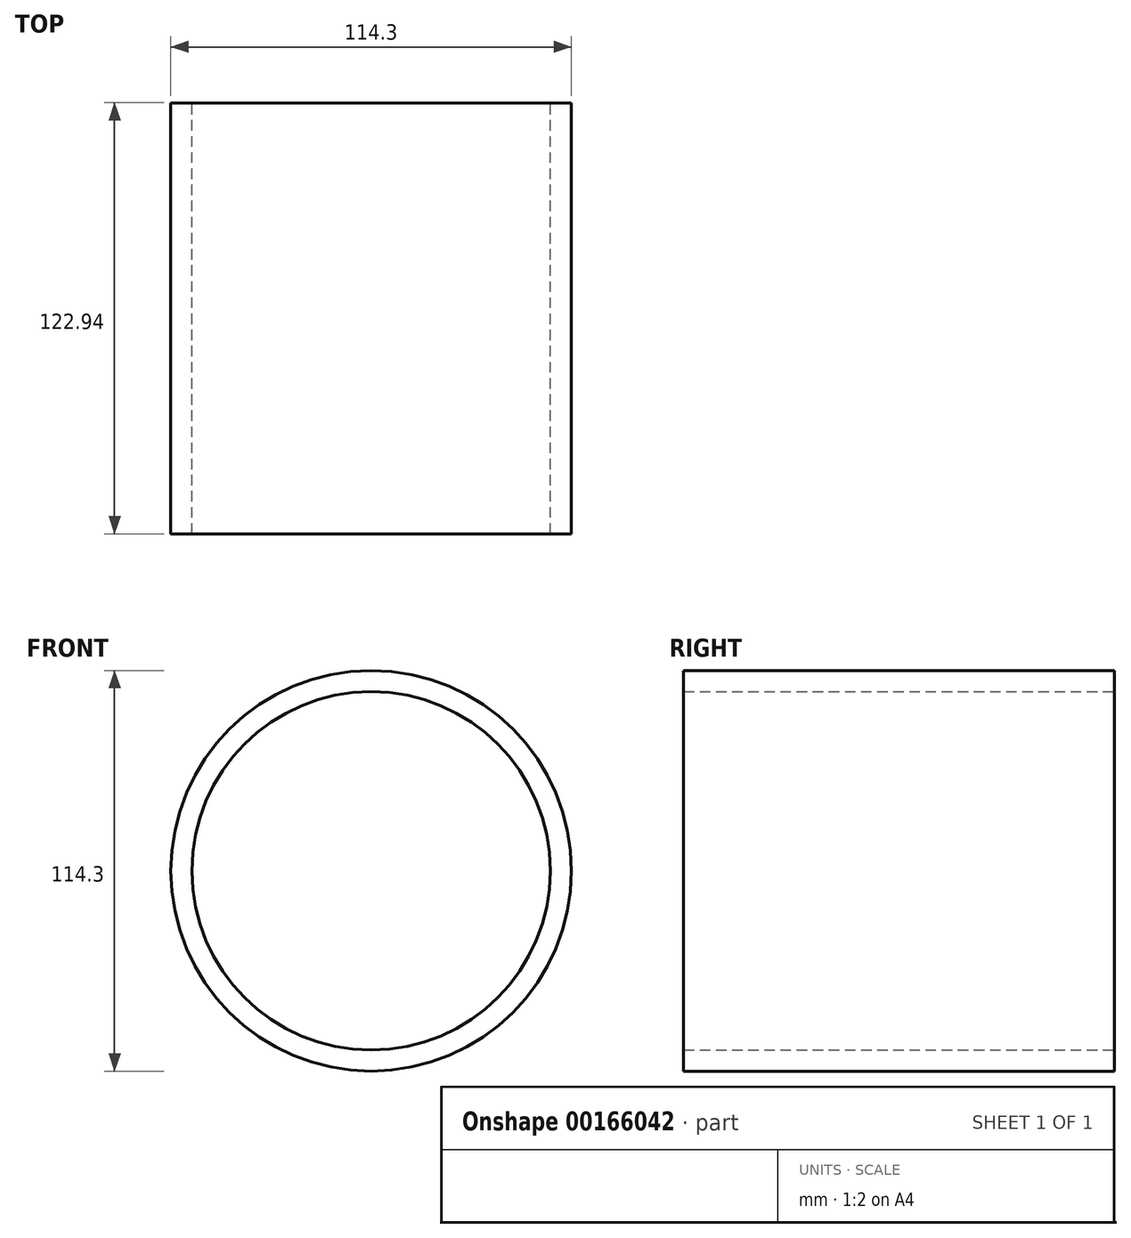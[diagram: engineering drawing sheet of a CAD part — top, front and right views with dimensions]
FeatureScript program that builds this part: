
annotation { "Feature Type Name" : "Feature", "Feature Type Description" : "" }
export const myFeature = defineFeature(function(context is Context, id is Id, definition is map)
    precondition{}
    {
        {
            var Q0;
            Q0=qCreatedBy(makeId("Front.planeOp"),FACE);
            var sketch = newSketch(context, id + "F0", { "sketchPlane" : qUnion([Q0])});
            skCircle(sketch, "E0", {"center": v(0, 0) * mm, "radius": 51.13 * mm});
            skCircle(sketch, "E1", {"center": v(0, 0) * mm, "radius": 57.15 * mm});
            skSolve(sketch);
        }
        {
            var Q0;
            Q0=makeQuery(id+"F0.imprint","IMPRINT",FACE,{"disambiguationData":[TD([[makeQuery(id+"F0.imprint","IMPRINT",EDGE,{"derivedFrom":sQuery(id+"F0.wireOp",EDGE,"E0")}),-1.0]])]});
            extrude(context, id + "F1", {"entities" : qUnion([Q0]), "endBound" : BoundingType.SYMMETRIC, "depth" : 122.94 * mm});
        }
    });
